# Revit family: Geräteeinsätze GES_Geräteeinsatz_GESRA9-10_mit_Griffbügel
name_source: partatom
category: Generic Models
revit_build: Autodesk Revit 2015 (Build: 20140606_1530(x64)
units: mm (PartAtom-declared; Revit-internal decimal feet)

## types (1)
- GESRA9 10U
    Article Type = GESRA9 10U
    Bodenbelagdicke = 10 mm  [stored 0.0328084 ft]
    Diameter dimesion = 305 mm  [stored 1.00066 ft]
    GTIN = 4012195104445
    Height = 71 mm  [stored 0.23294 ft]
    Inner cut = 287 mm
    Inner cut 3 = 232 mm
    Inner cut2 = 209 mm  [stored 0.685696 ft]
    Manufacturer = OBO Bettermann
    Manufacturer Art. No. = 7405580
    Material = Aluminum 6061
    Outer Diameter Dimension = 323 mm  [stored 1.05971 ft]
    Snur width = 111 mm
    URL = http://www.obo-bettermann.com

note: [stored X ft] marks values corroborated as IEEE doubles in the binary element streams (Revit-internal decimal feet)

## geometry (parser evidence)
native form markers: Sweep x2
no freeform markers — native parametric forms only
